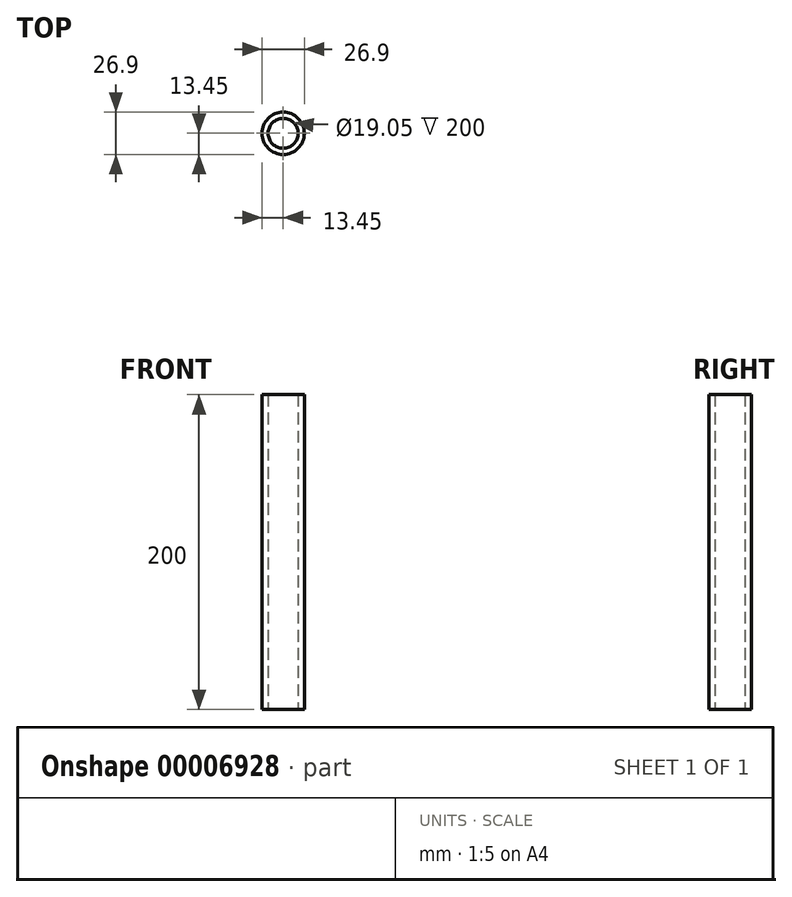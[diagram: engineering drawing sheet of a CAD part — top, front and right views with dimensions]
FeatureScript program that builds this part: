
annotation { "Feature Type Name" : "Feature", "Feature Type Description" : "" }
export const myFeature = defineFeature(function(context is Context, id is Id, definition is map)
    precondition{}
    {
        {
            var Q0;
            Q0=qCreatedBy(makeId("Top.planeOp"),FACE);
            var sketch = newSketch(context, id + "F0", { "sketchPlane" : qUnion([Q0])});
            skCircle(sketch, "E0", {"center": v(0, 0) * mm, "radius": 13.45 * mm});
            skCircle(sketch, "E1", {"center": v(0, 0) * mm, "radius": 9.53 * mm});
            skSolve(sketch);
        }
        {
            var Q0;
            Q0=makeQuery(id+"F0.imprint","IMPRINT",FACE,{"disambiguationData":[TD([[makeQuery(id+"F0.imprint","IMPRINT",EDGE,{"derivedFrom":sQuery(id+"F0.wireOp",EDGE,"E0")}),1.0]])]});
            extrude(context, id + "F1", {"entities" : qUnion([Q0]), "depth" : (200) * mm});
        }
    });
